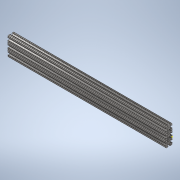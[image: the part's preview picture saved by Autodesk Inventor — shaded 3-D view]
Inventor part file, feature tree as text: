
AUTODESK INVENTOR PART (.ipt)
format: ipt  version: 2020 (Build 240168000, 168)  size: 391,680 bytes
history: native  units: in
note: dims shown in document units (in); Inventor stores cm internally (conversion verified against a paired STEP export)
features: sketch x2, extrude x1
ambient origin geometry x8: Origin, YZ Plane, XZ Plane, XY Plane, X Axis, Y Axis, Z Axis, Center Point
bodies: Solid1 (feature_tree)
feature tree (3):
  extrude  "Extrusion1"  [1 undecoded]
  sketch  "Sketch2"
  sketch  "Sketch1"  dims[d0=25.0in d1=0.0in]
note: 1 required parameter value undecoded (feature->parameter linkage not recoverable at this tier; creation-order binding heuristic only, values carry confidence <= 0.55)
